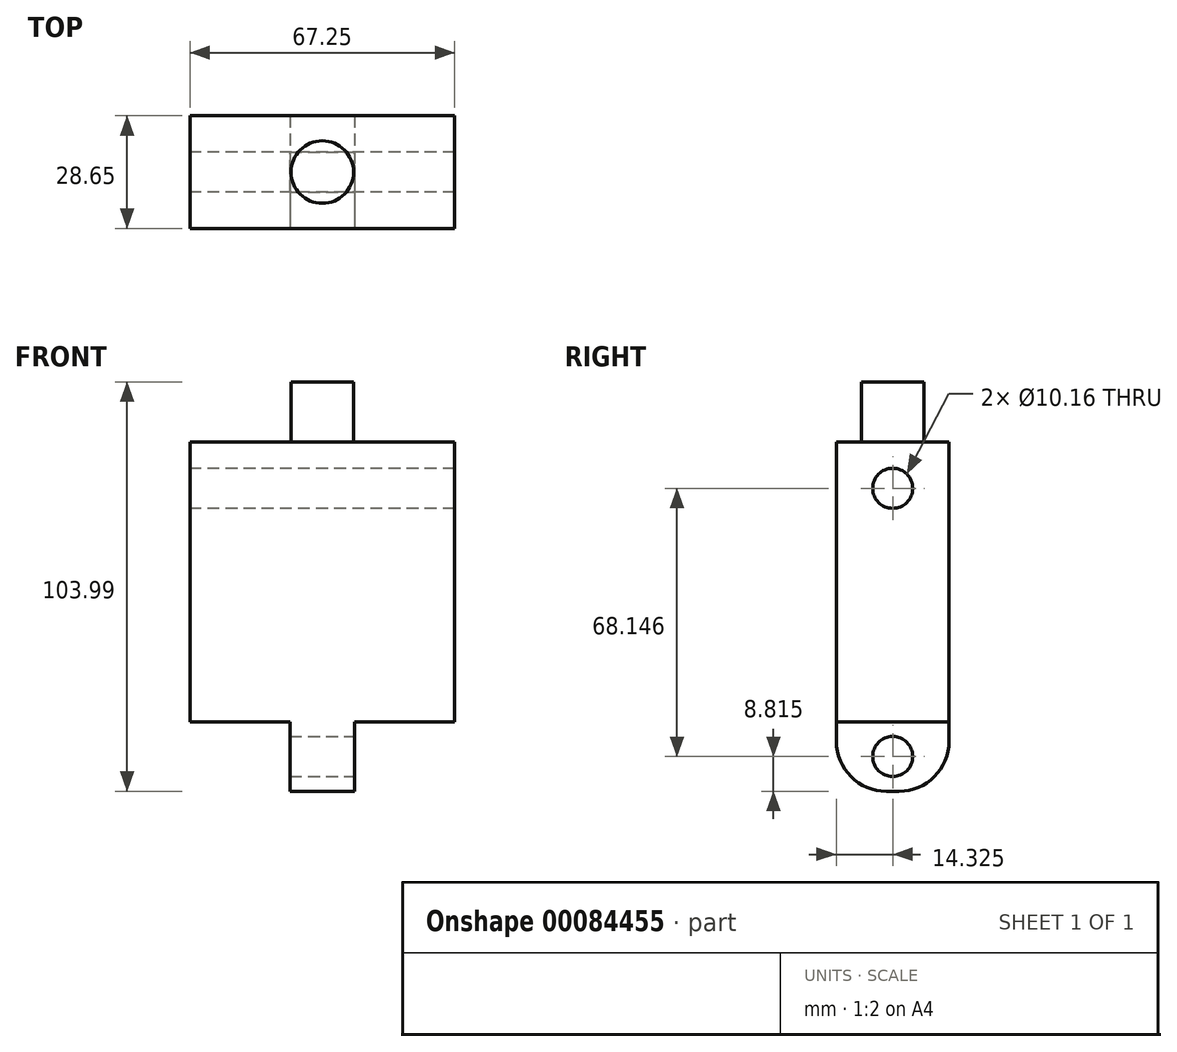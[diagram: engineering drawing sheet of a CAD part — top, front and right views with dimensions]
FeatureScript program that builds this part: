
annotation { "Feature Type Name" : "Feature", "Feature Type Description" : "" }
export const myFeature = defineFeature(function(context is Context, id is Id, definition is map)
    precondition{}
    {
        {
            var Q0;
            Q0=qCreatedBy(makeId("Top.planeOp"),FACE);
            var sketch = newSketch(context, id + "F0", { "sketchPlane" : qUnion([Q0])});
            skLineSegment(sketch, "E0.bottom", {"start": v(-67.25, 20.16) * mm, "end": v(0, 20.16) * mm});
            skLineSegment(sketch, "E0.top", {"start": v(-67.25, -8.49) * mm, "end": v(0, -8.49) * mm});
            skLineSegment(sketch, "E0.left", {"start": v(-67.25, 20.16) * mm, "end": v(-67.25, -8.49) * mm});
            skLineSegment(sketch, "E0.right", {"start": v(0, 20.16) * mm, "end": v(0, -8.49) * mm});
            skCircle(sketch, "E1", {"center": v(-33.63, 5.83) * mm, "radius": 7.94 * mm});
            skPoint(sketch, "E1.centerSnap0", {"position": v(-33.63, 20.16) * mm});
            skPoint(sketch, "E1.centerSnap1", {"position": v(-67.25, 5.83) * mm});
            skLineSegment(sketch, "E2", {"start": v(-33.63, 20.16) * mm, "end": v(-33.63, -8.49) * mm});
            skLineSegment(sketch, "E3", {"start": v(0, 12.64) * mm, "end": v(-25.4, 12.64) * mm});
            skLineSegment(sketch, "E4", {"start": v(-25.4, 20.16) * mm, "end": v(-25.4, -8.49) * mm});
            skLineSegment(sketch, "E5.MirrorCS", {"start": v(-41.85, 20.16) * mm, "end": v(-41.85, -8.49) * mm});
            skSolve(sketch);
        }
        {
            var Q0;
            Q0=makeQuery(id+"F0.imprint","IMPRINT",FACE,{"disambiguationData":[TD([[makeQuery(id+"F0.imprint","IMPRINT",EDGE,{"derivedFrom":sQuery(id+"F0.wireOp",EDGE,"E0.bottom")}),-1.0]])]});
            var Q1;
            {var subQ0=sQuery(id+"F0.wireOp",EDGE,"E0.right");var subQ3=makeQuery(id+"F0.imprint","IMPRINT",VERTEX,{"derivedFrom":subQ0});Q1=makeQuery(id+"F0.imprint","IMPRINT",FACE,{"disambiguationData":[TD([[makeQuery(id+"F0.imprint","IMPRINT",EDGE,{"disambiguationData":[TD([[subQ3,1.0]])],"derivedFrom":subQ0}),-1.0]])]});}
            var Q2;
            {var subQ4=sQuery(id+"F0.wireOp",EDGE,"E0.left");Q2=makeQuery(id+"F0.imprint","IMPRINT",FACE,{"disambiguationData":[TD([[makeQuery(id+"F0.imprint","IMPRINT",EDGE,{"derivedFrom":subQ4}),1.0]])]});}
            var Q3;
            {var subQ0=sQuery(id+"F0.wireOp",EDGE,"E2");var subQ1=sQuery(id+"F0.wireOp",EDGE,"E0.bottom");var subQ2=makeQuery(id+"F0.imprint","INTERSECT",VERTEX,{"derivedFrom":[subQ1,subQ0]});Q3=makeQuery(id+"F0.imprint","IMPRINT",FACE,{"disambiguationData":[TD([[makeQuery(id+"F0.imprint","IMPRINT",EDGE,{"disambiguationData":[TD([[subQ2,-1.0]])],"derivedFrom":subQ1}),-1.0]])]});}
            var Q4;
            {var subQ5=sQuery(id+"F0.wireOp",EDGE,"E3");Q4=makeQuery(id+"F0.imprint","IMPRINT",FACE,{"disambiguationData":[TD([[makeQuery(id+"F0.imprint","IMPRINT",EDGE,{"derivedFrom":subQ5}),1.0]])]});}
            var Q5;
            {var subQ8=sQuery(id+"F0.wireOp",EDGE,"E5.MirrorCS");Q5=makeQuery(id+"F0.imprint","IMPRINT",FACE,{"disambiguationData":[TD([[makeQuery(id+"F0.imprint","IMPRINT",EDGE,{"derivedFrom":subQ8}),1.0]])]});}
            extrude(context, id + "F1", {"entities" : qUnion([Q0, Q1, Q2, Q3, Q4, Q5]), "depth" : 71.12 * mm});
        }
        {
            var Q0;
            Q0=makeQuery(id+"F0.imprint","IMPRINT",FACE,{"disambiguationData":[TD([[makeQuery(id+"F0.imprint","IMPRINT",EDGE,{"derivedFrom":sQuery(id+"F0.wireOp",EDGE,"E1")}),1.0]])]});
            extrude(context, id + "F2", {"entities" : qUnion([Q0]), "operationType" : NewBodyOperationType.ADD, "depth" : 86.36 * mm});
        }
        {
            var Q0;
            {var subQ0=sQuery(id+"F0.wireOp",EDGE,"E2");var subQ1=sQuery(id+"F0.wireOp",EDGE,"E1");var subQ2=makeQuery(id+"F0.imprint","INTERSECT",VERTEX,{"disambiguationData":[OD(0.0)],"derivedFrom":[subQ1,subQ0]});Q0=makeQuery(id+"F0.imprint","IMPRINT",FACE,{"disambiguationData":[TD([[makeQuery(id+"F0.imprint","IMPRINT",EDGE,{"disambiguationData":[TD([[subQ2,1.0]])],"derivedFrom":subQ1}),1.0]])]});}
            var Q1;
            {var subQ0=sQuery(id+"F0.wireOp",EDGE,"E2");var subQ1=sQuery(id+"F0.wireOp",EDGE,"E0.bottom");var subQ2=makeQuery(id+"F0.imprint","INTERSECT",VERTEX,{"derivedFrom":[subQ1,subQ0]});Q1=makeQuery(id+"F0.imprint","IMPRINT",FACE,{"disambiguationData":[TD([[makeQuery(id+"F0.imprint","IMPRINT",EDGE,{"disambiguationData":[TD([[subQ2,-1.0]])],"derivedFrom":subQ1}),-1.0]])]});}
            var Q2;
            {var subQ8=sQuery(id+"F0.wireOp",EDGE,"E5.MirrorCS");Q2=makeQuery(id+"F0.imprint","IMPRINT",FACE,{"disambiguationData":[TD([[makeQuery(id+"F0.imprint","IMPRINT",EDGE,{"derivedFrom":subQ8}),1.0]])]});}
            var Q3;
            {var subQ0=sQuery(id+"F0.wireOp",EDGE,"E2");var subQ1=sQuery(id+"F0.wireOp",EDGE,"E1");var subQ2=makeQuery(id+"F0.imprint","INTERSECT",VERTEX,{"disambiguationData":[OD(0.0)],"derivedFrom":[subQ1,subQ0]});Q3=makeQuery(id+"F0.imprint","IMPRINT",FACE,{"disambiguationData":[TD([[makeQuery(id+"F0.imprint","IMPRINT",EDGE,{"disambiguationData":[TD([[subQ2,-1.0]])],"derivedFrom":subQ1}),1.0]])]});}
            extrude(context, id + "F3", {"entities" : qUnion([Q0, Q1, Q2, Q3]), "operationType" : NewBodyOperationType.ADD, "oppositeDirection" : true, "depth" : 17.63 * mm});
        }
        {
            var Q0;
            Q0=makeQuery(id+"F3.opExtrude","CAP_EDGE",EDGE,{"disambiguationData":[OSD([sQuery(id+"F0.wireOp",EDGE,"E0.top")])],"isStart":false});
            var Q1;
            Q1=makeQuery(id+"F3.opExtrude","CAP_EDGE",EDGE,{"disambiguationData":[OSD([sQuery(id+"F0.wireOp",EDGE,"E0.bottom")])],"isStart":false});
            fillet(context, id + "F4", {"entities" : qUnion([Q0, Q1]), "radius" : 12.7 * mm, "tangentPropagation" : true, "allowEdgeOverflow" : false});
        }
        {
            var Q0;
            Q0=makeQuery(id+"F3.opExtrude","SWEPT_FACE",FACE,{"disambiguationData":[OSD([sQuery(id+"F0.wireOp",EDGE,"E5.MirrorCS")])]});
            var sketch = newSketch(context, id + "F5", { "sketchPlane" : qUnion([Q0])});
            skLineSegment(sketch, "E6", {"start": v(-5.83, 0) * mm, "end": v(-5.83, -17.63) * mm});
            skCircle(sketch, "E7", {"center": v(-5.83, -8.81) * mm, "radius": 4.57 * mm});
            skSolve(sketch);
        }
        {
            var Q0;
            Q0=sQuery(id+"F5.wireOp",VERTEX,"E7.center");
            var Q1;
            Q1=makeQuery(id+"F1.opExtrude","SWEPT_BODY",BODY,{"disambiguationData":[OSD([sQuery(id+"F0.wireOp",EDGE,"E0.bottom"),sQuery(id+"F0.wireOp",EDGE,"E0.top"),sQuery(id+"F0.wireOp",EDGE,"E0.left"),sQuery(id+"F0.wireOp",EDGE,"E0.right"),sQuery(id+"F0.wireOp",EDGE,"E1")])]});
            hole(context, id + "F6", {"style" : HoleStyle.SIMPLE, "endStyle" : HoleEndStyle.THROUGH, "holeDiameter" : 10.16 * mm, "locations" : qUnion([Q0]), "scope" : qUnion([Q1]), "isTappedThrough" : true});
        }
        {
            var Q0;
            Q0=makeQuery(id+"F1.opExtrude","SWEPT_FACE",FACE,{"disambiguationData":[OSD([sQuery(id+"F0.wireOp",EDGE,"E0.right")])]});
            var sketch = newSketch(context, id + "F7", { "sketchPlane" : qUnion([Q0])});
            skCircle(sketch, "E8", {"center": v(5.83, 59.33) * mm, "radius": 5.08 * mm});
            skPoint(sketch, "E8.centerSnap0", {"position": v(5.83, 71.12) * mm});
            skSolve(sketch);
        }
        {
            var Q0;
            Q0=sQuery(id+"F7.wireOp",VERTEX,"E8.center");
            var Q1;
            Q1=makeQuery(id+"F1.opExtrude","SWEPT_BODY",BODY,{"disambiguationData":[OSD([sQuery(id+"F0.wireOp",EDGE,"E0.bottom"),sQuery(id+"F0.wireOp",EDGE,"E0.top"),sQuery(id+"F0.wireOp",EDGE,"E0.left"),sQuery(id+"F0.wireOp",EDGE,"E0.right"),sQuery(id+"F0.wireOp",EDGE,"E1")])]});
            hole(context, id + "F8", {"style" : HoleStyle.SIMPLE, "endStyle" : HoleEndStyle.THROUGH, "holeDiameter" : 10.16 * mm, "locations" : qUnion([Q0]), "scope" : qUnion([Q1]), "isTappedThrough" : true});
        }
    });
